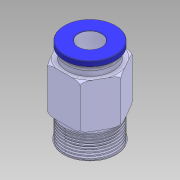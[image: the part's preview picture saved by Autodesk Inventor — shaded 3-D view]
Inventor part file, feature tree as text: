
AUTODESK INVENTOR PART (.ipt)
format: ipt  version: 2019 (Build 230136000, 136)  size: 583,680 bytes
history: native  units: mm
features: other x3, sketch x1
ambient origin geometry x8: Origin, YZ Plane, XZ Plane, XY Plane, X Axis, Y Axis, Z Axis, Center Point
bodies: Body1 (feature_tree)
feature tree (4):
  other  "Sólido1"
  other  "Geometría reparada1"
  sketch  "Boceto 3D1"
  other  "PartBody"
